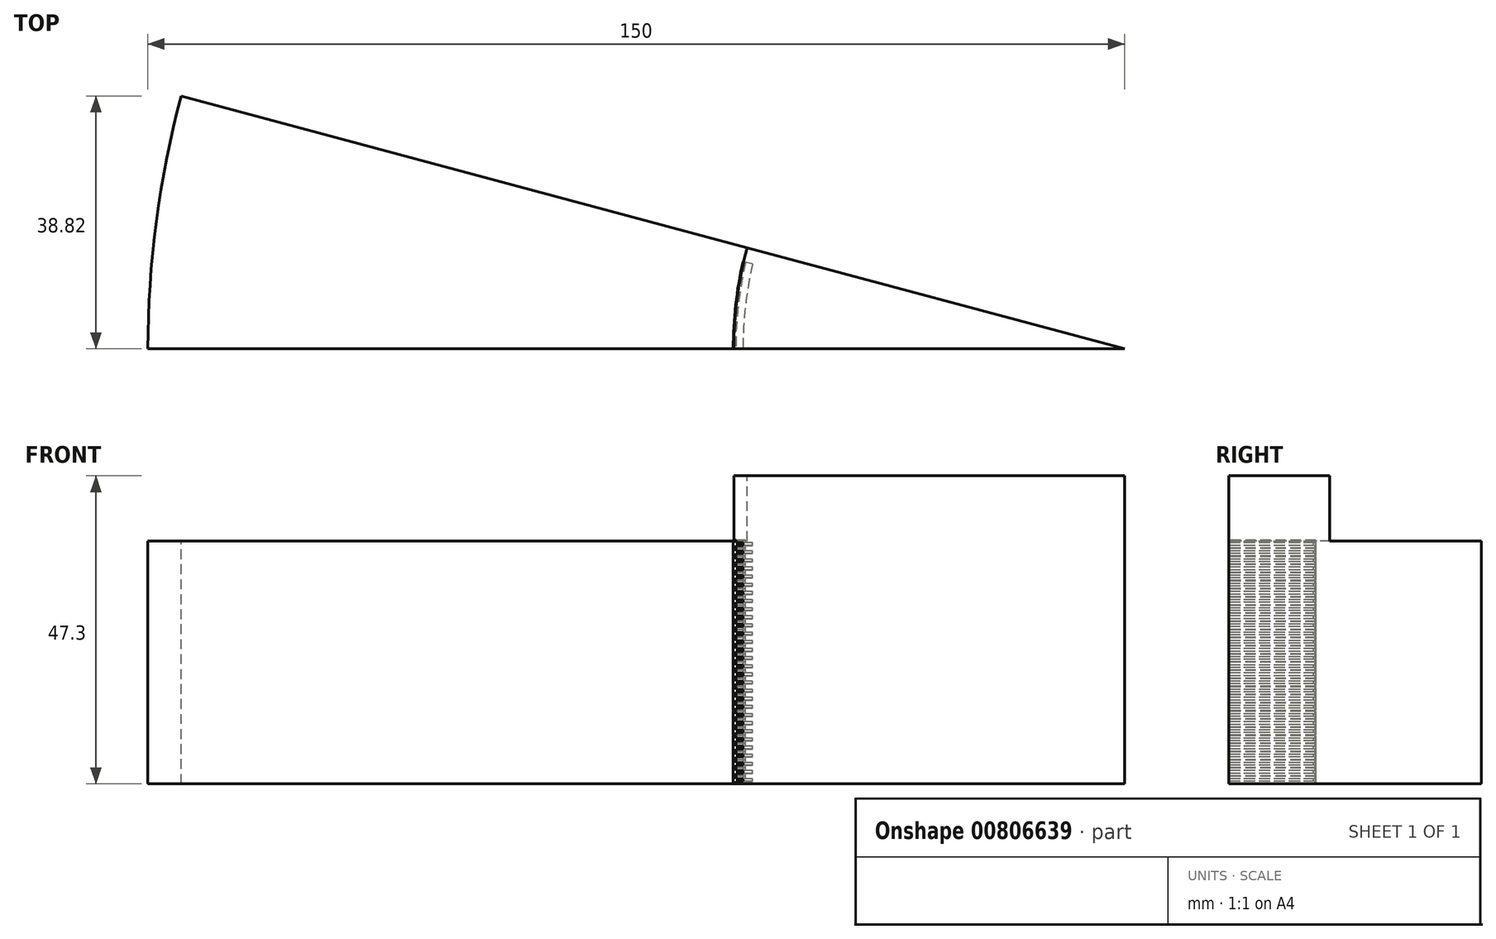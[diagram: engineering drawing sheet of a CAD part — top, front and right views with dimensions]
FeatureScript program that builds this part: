
annotation { "Feature Type Name" : "Feature", "Feature Type Description" : "" }
export const myFeature = defineFeature(function(context is Context, id is Id, definition is map)
    precondition{}
    {
        {
            var Q0;
            Q0=qCreatedBy(makeId("Front.planeOp"),FACE);
            var sketch = newSketch(context, id + "F0", { "sketchPlane" : qUnion([Q0])});
            skLineSegment(sketch, "E0", {"start": v(0, 0) * mm, "end": v(-150, 0) * mm});
            skLineSegment(sketch, "E1", {"start": v(-150, 0) * mm, "end": v(-150, 37.3) * mm});
            skLineSegment(sketch, "E2", {"start": v(-60, 37.3) * mm, "end": v(-60, 47.3) * mm});
            skLineSegment(sketch, "E3", {"start": v(-60, 47.3) * mm, "end": v(0, 47.3) * mm});
            skLineSegment(sketch, "E4", {"start": v(0, 47.3) * mm, "end": v(0, 0) * mm});
            skLineSegment(sketch, "E5", {"start": v(-150, 37.3) * mm, "end": v(-60, 37.3) * mm});
            skSolve(sketch);
        }
        {
            var Q0;
            Q0 = qSketchRegion(id + "F0", true);
            var Q1;
            Q1=sQuery(id+"F0.wireOp",EDGE,"E4");
            revolve(context, id + "F1", {"surfaceOperationType" : NewSurfaceOperationType.NEW, "entities" : qUnion([Q0]), "axis" : qUnion([Q1]), "revolveType" : RevolveType.ONE_DIRECTION, "angle" : 15 * degree});
        }
        {
            var Q0;
            Q0=makeQuery(id+"F1.opRevolve","CAP_FACE",FACE,{"disambiguationData":[OSD([sQuery(id+"F0.wireOp",EDGE,"E0"),sQuery(id+"F0.wireOp",EDGE,"E1"),sQuery(id+"F0.wireOp",EDGE,"E2"),sQuery(id+"F0.wireOp",EDGE,"E3"),sQuery(id+"F0.wireOp",EDGE,"E4"),sQuery(id+"F0.wireOp",EDGE,"E5")])],"isStart":true});
            var sketch = newSketch(context, id + "F2", { "sketchPlane" : qUnion([Q0])});
            skLineSegment(sketch, "E6", {"start": v(-60.1, 37.4) * mm, "end": v(-60.1, 36.23) * mm});
            skLineSegment(sketch, "E7", {"start": v(-60.1, 36.23) * mm, "end": v(-59.7, 36.23) * mm});
            skLineSegment(sketch, "E8", {"start": v(-59.7, 36.23) * mm, "end": v(-59.7, 36.61) * mm});
            skLineSegment(sketch, "E9", {"start": v(-59.7, 36.61) * mm, "end": v(-58.6, 36.61) * mm});
            skLineSegment(sketch, "E10", {"start": v(-58.6, 36.61) * mm, "end": v(-58.6, 37.01) * mm});
            skLineSegment(sketch, "E11", {"start": v(-58.6, 37.01) * mm, "end": v(-59.7, 37.01) * mm});
            skLineSegment(sketch, "E12", {"start": v(-59.7, 37.01) * mm, "end": v(-59.7, 37.4) * mm});
            skLineSegment(sketch, "E13", {"start": v(-59.7, 37.4) * mm, "end": v(-60.1, 37.4) * mm});
            skLineSegment(sketch, "E14.1.0.0", {"start": v(-59.7, 35.76) * mm, "end": v(-59.7, 36.15) * mm});
            skLineSegment(sketch, "E14.1.0.1", {"start": v(-58.6, 35.76) * mm, "end": v(-59.7, 35.76) * mm});
            skLineSegment(sketch, "E14.1.0.2", {"start": v(-58.6, 35.36) * mm, "end": v(-58.6, 35.76) * mm});
            skLineSegment(sketch, "E14.1.0.3", {"start": v(-59.7, 35.36) * mm, "end": v(-58.6, 35.36) * mm});
            skLineSegment(sketch, "E14.1.0.4", {"start": v(-59.7, 34.98) * mm, "end": v(-59.7, 35.36) * mm});
            skLineSegment(sketch, "E14.1.0.5", {"start": v(-60.1, 34.98) * mm, "end": v(-59.7, 34.98) * mm});
            skLineSegment(sketch, "E14.1.0.6", {"start": v(-60.1, 36.15) * mm, "end": v(-60.1, 34.98) * mm});
            skLineSegment(sketch, "E14.1.0.7", {"start": v(-59.7, 36.15) * mm, "end": v(-60.1, 36.15) * mm});
            skLineSegment(sketch, "E14.2.0.0", {"start": v(-59.7, 34.51) * mm, "end": v(-59.7, 34.9) * mm});
            skLineSegment(sketch, "E14.2.0.1", {"start": v(-58.6, 34.51) * mm, "end": v(-59.7, 34.51) * mm});
            skLineSegment(sketch, "E14.2.0.2", {"start": v(-58.6, 34.11) * mm, "end": v(-58.6, 34.51) * mm});
            skLineSegment(sketch, "E14.2.0.3", {"start": v(-59.7, 34.11) * mm, "end": v(-58.6, 34.11) * mm});
            skLineSegment(sketch, "E14.2.0.4", {"start": v(-59.7, 33.73) * mm, "end": v(-59.7, 34.11) * mm});
            skLineSegment(sketch, "E14.2.0.5", {"start": v(-60.1, 33.73) * mm, "end": v(-59.7, 33.73) * mm});
            skLineSegment(sketch, "E14.2.0.6", {"start": v(-60.1, 34.9) * mm, "end": v(-60.1, 33.73) * mm});
            skLineSegment(sketch, "E14.2.0.7", {"start": v(-59.7, 34.9) * mm, "end": v(-60.1, 34.9) * mm});
            skLineSegment(sketch, "E14.direction1", {"start": v(-60.1, 36.23) * mm, "end": v(-60.1, 34.98) * mm, "construction": true});
            skLineSegment(sketch, "E15.0.3.0", {"start": v(-59.7, 33.26) * mm, "end": v(-59.7, 33.65) * mm});
            skLineSegment(sketch, "E15.3.3.0", {"start": v(-58.6, 33.26) * mm, "end": v(-59.7, 33.26) * mm});
            skLineSegment(sketch, "E15.6.3.0", {"start": v(-58.6, 32.86) * mm, "end": v(-58.6, 33.26) * mm});
            skLineSegment(sketch, "E15.9.3.0", {"start": v(-59.7, 32.86) * mm, "end": v(-58.6, 32.86) * mm});
            skLineSegment(sketch, "E15.12.3.0", {"start": v(-59.7, 32.48) * mm, "end": v(-59.7, 32.86) * mm});
            skLineSegment(sketch, "E15.15.3.0", {"start": v(-60.1, 32.48) * mm, "end": v(-59.7, 32.48) * mm});
            skLineSegment(sketch, "E15.18.3.0", {"start": v(-60.1, 33.65) * mm, "end": v(-60.1, 32.48) * mm});
            skLineSegment(sketch, "E15.21.3.0", {"start": v(-59.7, 33.65) * mm, "end": v(-60.1, 33.65) * mm});
            skLineSegment(sketch, "E15.0.4.0", {"start": v(-59.7, 32.01) * mm, "end": v(-59.7, 32.4) * mm});
            skLineSegment(sketch, "E15.3.4.0", {"start": v(-58.6, 32.01) * mm, "end": v(-59.7, 32.01) * mm});
            skLineSegment(sketch, "E15.6.4.0", {"start": v(-58.6, 31.61) * mm, "end": v(-58.6, 32.01) * mm});
            skLineSegment(sketch, "E15.9.4.0", {"start": v(-59.7, 31.61) * mm, "end": v(-58.6, 31.61) * mm});
            skLineSegment(sketch, "E15.12.4.0", {"start": v(-59.7, 31.23) * mm, "end": v(-59.7, 31.61) * mm});
            skLineSegment(sketch, "E15.15.4.0", {"start": v(-60.1, 31.23) * mm, "end": v(-59.7, 31.23) * mm});
            skLineSegment(sketch, "E15.18.4.0", {"start": v(-60.1, 32.4) * mm, "end": v(-60.1, 31.23) * mm});
            skLineSegment(sketch, "E15.21.4.0", {"start": v(-59.7, 32.4) * mm, "end": v(-60.1, 32.4) * mm});
            skLineSegment(sketch, "E15.0.5.0", {"start": v(-59.7, 30.76) * mm, "end": v(-59.7, 31.15) * mm});
            skLineSegment(sketch, "E15.3.5.0", {"start": v(-58.6, 30.76) * mm, "end": v(-59.7, 30.76) * mm});
            skLineSegment(sketch, "E15.6.5.0", {"start": v(-58.6, 30.36) * mm, "end": v(-58.6, 30.76) * mm});
            skLineSegment(sketch, "E15.9.5.0", {"start": v(-59.7, 30.36) * mm, "end": v(-58.6, 30.36) * mm});
            skLineSegment(sketch, "E15.12.5.0", {"start": v(-59.7, 29.98) * mm, "end": v(-59.7, 30.36) * mm});
            skLineSegment(sketch, "E15.15.5.0", {"start": v(-60.1, 29.98) * mm, "end": v(-59.7, 29.98) * mm});
            skLineSegment(sketch, "E15.18.5.0", {"start": v(-60.1, 31.15) * mm, "end": v(-60.1, 29.98) * mm});
            skLineSegment(sketch, "E15.21.5.0", {"start": v(-59.7, 31.15) * mm, "end": v(-60.1, 31.15) * mm});
            skLineSegment(sketch, "E15.0.6.0", {"start": v(-59.7, 29.51) * mm, "end": v(-59.7, 29.9) * mm});
            skLineSegment(sketch, "E15.3.6.0", {"start": v(-58.6, 29.51) * mm, "end": v(-59.7, 29.51) * mm});
            skLineSegment(sketch, "E15.6.6.0", {"start": v(-58.6, 29.11) * mm, "end": v(-58.6, 29.51) * mm});
            skLineSegment(sketch, "E15.9.6.0", {"start": v(-59.7, 29.11) * mm, "end": v(-58.6, 29.11) * mm});
            skLineSegment(sketch, "E15.12.6.0", {"start": v(-59.7, 28.73) * mm, "end": v(-59.7, 29.11) * mm});
            skLineSegment(sketch, "E15.15.6.0", {"start": v(-60.1, 28.73) * mm, "end": v(-59.7, 28.73) * mm});
            skLineSegment(sketch, "E15.18.6.0", {"start": v(-60.1, 29.9) * mm, "end": v(-60.1, 28.73) * mm});
            skLineSegment(sketch, "E15.21.6.0", {"start": v(-59.7, 29.9) * mm, "end": v(-60.1, 29.9) * mm});
            skLineSegment(sketch, "E15.0.7.0", {"start": v(-59.7, 28.26) * mm, "end": v(-59.7, 28.65) * mm});
            skLineSegment(sketch, "E15.3.7.0", {"start": v(-58.6, 28.26) * mm, "end": v(-59.7, 28.26) * mm});
            skLineSegment(sketch, "E15.6.7.0", {"start": v(-58.6, 27.86) * mm, "end": v(-58.6, 28.26) * mm});
            skLineSegment(sketch, "E15.9.7.0", {"start": v(-59.7, 27.86) * mm, "end": v(-58.6, 27.86) * mm});
            skLineSegment(sketch, "E15.12.7.0", {"start": v(-59.7, 27.48) * mm, "end": v(-59.7, 27.86) * mm});
            skLineSegment(sketch, "E15.15.7.0", {"start": v(-60.1, 27.48) * mm, "end": v(-59.7, 27.48) * mm});
            skLineSegment(sketch, "E15.18.7.0", {"start": v(-60.1, 28.65) * mm, "end": v(-60.1, 27.48) * mm});
            skLineSegment(sketch, "E15.21.7.0", {"start": v(-59.7, 28.65) * mm, "end": v(-60.1, 28.65) * mm});
            skLineSegment(sketch, "E15.0.8.0", {"start": v(-59.7, 27.01) * mm, "end": v(-59.7, 27.4) * mm});
            skLineSegment(sketch, "E15.3.8.0", {"start": v(-58.6, 27.01) * mm, "end": v(-59.7, 27.01) * mm});
            skLineSegment(sketch, "E15.6.8.0", {"start": v(-58.6, 26.61) * mm, "end": v(-58.6, 27.01) * mm});
            skLineSegment(sketch, "E15.9.8.0", {"start": v(-59.7, 26.61) * mm, "end": v(-58.6, 26.61) * mm});
            skLineSegment(sketch, "E15.12.8.0", {"start": v(-59.7, 26.23) * mm, "end": v(-59.7, 26.61) * mm});
            skLineSegment(sketch, "E15.15.8.0", {"start": v(-60.1, 26.23) * mm, "end": v(-59.7, 26.23) * mm});
            skLineSegment(sketch, "E15.18.8.0", {"start": v(-60.1, 27.4) * mm, "end": v(-60.1, 26.23) * mm});
            skLineSegment(sketch, "E15.21.8.0", {"start": v(-59.7, 27.4) * mm, "end": v(-60.1, 27.4) * mm});
            skLineSegment(sketch, "E15.0.9.0", {"start": v(-59.7, 25.76) * mm, "end": v(-59.7, 26.15) * mm});
            skLineSegment(sketch, "E15.3.9.0", {"start": v(-58.6, 25.76) * mm, "end": v(-59.7, 25.76) * mm});
            skLineSegment(sketch, "E15.6.9.0", {"start": v(-58.6, 25.36) * mm, "end": v(-58.6, 25.76) * mm});
            skLineSegment(sketch, "E15.9.9.0", {"start": v(-59.7, 25.36) * mm, "end": v(-58.6, 25.36) * mm});
            skLineSegment(sketch, "E15.12.9.0", {"start": v(-59.7, 24.98) * mm, "end": v(-59.7, 25.36) * mm});
            skLineSegment(sketch, "E15.15.9.0", {"start": v(-60.1, 24.98) * mm, "end": v(-59.7, 24.98) * mm});
            skLineSegment(sketch, "E15.18.9.0", {"start": v(-60.1, 26.15) * mm, "end": v(-60.1, 24.98) * mm});
            skLineSegment(sketch, "E15.21.9.0", {"start": v(-59.7, 26.15) * mm, "end": v(-60.1, 26.15) * mm});
            skLineSegment(sketch, "E16.0.10.0", {"start": v(-59.7, 24.51) * mm, "end": v(-59.7, 24.9) * mm});
            skLineSegment(sketch, "E16.3.10.0", {"start": v(-58.6, 24.51) * mm, "end": v(-59.7, 24.51) * mm});
            skLineSegment(sketch, "E16.6.10.0", {"start": v(-58.6, 24.11) * mm, "end": v(-58.6, 24.51) * mm});
            skLineSegment(sketch, "E16.9.10.0", {"start": v(-59.7, 24.11) * mm, "end": v(-58.6, 24.11) * mm});
            skLineSegment(sketch, "E16.12.10.0", {"start": v(-59.7, 23.73) * mm, "end": v(-59.7, 24.11) * mm});
            skLineSegment(sketch, "E16.15.10.0", {"start": v(-60.1, 23.73) * mm, "end": v(-59.7, 23.73) * mm});
            skLineSegment(sketch, "E16.18.10.0", {"start": v(-60.1, 24.9) * mm, "end": v(-60.1, 23.73) * mm});
            skLineSegment(sketch, "E16.21.10.0", {"start": v(-59.7, 24.9) * mm, "end": v(-60.1, 24.9) * mm});
            skLineSegment(sketch, "E16.0.11.0", {"start": v(-59.7, 23.26) * mm, "end": v(-59.7, 23.65) * mm});
            skLineSegment(sketch, "E16.3.11.0", {"start": v(-58.6, 23.26) * mm, "end": v(-59.7, 23.26) * mm});
            skLineSegment(sketch, "E16.6.11.0", {"start": v(-58.6, 22.86) * mm, "end": v(-58.6, 23.26) * mm});
            skLineSegment(sketch, "E16.9.11.0", {"start": v(-59.7, 22.86) * mm, "end": v(-58.6, 22.86) * mm});
            skLineSegment(sketch, "E16.12.11.0", {"start": v(-59.7, 22.48) * mm, "end": v(-59.7, 22.86) * mm});
            skLineSegment(sketch, "E16.15.11.0", {"start": v(-60.1, 22.48) * mm, "end": v(-59.7, 22.48) * mm});
            skLineSegment(sketch, "E16.18.11.0", {"start": v(-60.1, 23.65) * mm, "end": v(-60.1, 22.48) * mm});
            skLineSegment(sketch, "E16.21.11.0", {"start": v(-59.7, 23.65) * mm, "end": v(-60.1, 23.65) * mm});
            skLineSegment(sketch, "E16.0.12.0", {"start": v(-59.7, 22.01) * mm, "end": v(-59.7, 22.4) * mm});
            skLineSegment(sketch, "E16.3.12.0", {"start": v(-58.6, 22.01) * mm, "end": v(-59.7, 22.01) * mm});
            skLineSegment(sketch, "E16.6.12.0", {"start": v(-58.6, 21.61) * mm, "end": v(-58.6, 22.01) * mm});
            skLineSegment(sketch, "E16.9.12.0", {"start": v(-59.7, 21.61) * mm, "end": v(-58.6, 21.61) * mm});
            skLineSegment(sketch, "E16.12.12.0", {"start": v(-59.7, 21.23) * mm, "end": v(-59.7, 21.61) * mm});
            skLineSegment(sketch, "E16.15.12.0", {"start": v(-60.1, 21.23) * mm, "end": v(-59.7, 21.23) * mm});
            skLineSegment(sketch, "E16.18.12.0", {"start": v(-60.1, 22.4) * mm, "end": v(-60.1, 21.23) * mm});
            skLineSegment(sketch, "E16.21.12.0", {"start": v(-59.7, 22.4) * mm, "end": v(-60.1, 22.4) * mm});
            skLineSegment(sketch, "E16.0.13.0", {"start": v(-59.7, 20.76) * mm, "end": v(-59.7, 21.15) * mm});
            skLineSegment(sketch, "E16.3.13.0", {"start": v(-58.6, 20.76) * mm, "end": v(-59.7, 20.76) * mm});
            skLineSegment(sketch, "E16.6.13.0", {"start": v(-58.6, 20.36) * mm, "end": v(-58.6, 20.76) * mm});
            skLineSegment(sketch, "E16.9.13.0", {"start": v(-59.7, 20.36) * mm, "end": v(-58.6, 20.36) * mm});
            skLineSegment(sketch, "E16.12.13.0", {"start": v(-59.7, 19.98) * mm, "end": v(-59.7, 20.36) * mm});
            skLineSegment(sketch, "E16.15.13.0", {"start": v(-60.1, 19.98) * mm, "end": v(-59.7, 19.98) * mm});
            skLineSegment(sketch, "E16.18.13.0", {"start": v(-60.1, 21.15) * mm, "end": v(-60.1, 19.98) * mm});
            skLineSegment(sketch, "E16.21.13.0", {"start": v(-59.7, 21.15) * mm, "end": v(-60.1, 21.15) * mm});
            skLineSegment(sketch, "E16.0.14.0", {"start": v(-59.7, 19.51) * mm, "end": v(-59.7, 19.9) * mm});
            skLineSegment(sketch, "E16.3.14.0", {"start": v(-58.6, 19.51) * mm, "end": v(-59.7, 19.51) * mm});
            skLineSegment(sketch, "E16.6.14.0", {"start": v(-58.6, 19.11) * mm, "end": v(-58.6, 19.51) * mm});
            skLineSegment(sketch, "E16.9.14.0", {"start": v(-59.7, 19.11) * mm, "end": v(-58.6, 19.11) * mm});
            skLineSegment(sketch, "E16.12.14.0", {"start": v(-59.7, 18.73) * mm, "end": v(-59.7, 19.11) * mm});
            skLineSegment(sketch, "E16.15.14.0", {"start": v(-60.1, 18.73) * mm, "end": v(-59.7, 18.73) * mm});
            skLineSegment(sketch, "E16.18.14.0", {"start": v(-60.1, 19.9) * mm, "end": v(-60.1, 18.73) * mm});
            skLineSegment(sketch, "E16.21.14.0", {"start": v(-59.7, 19.9) * mm, "end": v(-60.1, 19.9) * mm});
            skLineSegment(sketch, "E16.0.15.0", {"start": v(-59.7, 18.26) * mm, "end": v(-59.7, 18.65) * mm});
            skLineSegment(sketch, "E16.3.15.0", {"start": v(-58.6, 18.26) * mm, "end": v(-59.7, 18.26) * mm});
            skLineSegment(sketch, "E16.6.15.0", {"start": v(-58.6, 17.86) * mm, "end": v(-58.6, 18.26) * mm});
            skLineSegment(sketch, "E16.9.15.0", {"start": v(-59.7, 17.86) * mm, "end": v(-58.6, 17.86) * mm});
            skLineSegment(sketch, "E16.12.15.0", {"start": v(-59.7, 17.48) * mm, "end": v(-59.7, 17.86) * mm});
            skLineSegment(sketch, "E16.15.15.0", {"start": v(-60.1, 17.48) * mm, "end": v(-59.7, 17.48) * mm});
            skLineSegment(sketch, "E16.18.15.0", {"start": v(-60.1, 18.65) * mm, "end": v(-60.1, 17.48) * mm});
            skLineSegment(sketch, "E16.21.15.0", {"start": v(-59.7, 18.65) * mm, "end": v(-60.1, 18.65) * mm});
            skLineSegment(sketch, "E16.0.16.0", {"start": v(-59.7, 17.01) * mm, "end": v(-59.7, 17.4) * mm});
            skLineSegment(sketch, "E16.3.16.0", {"start": v(-58.6, 17.01) * mm, "end": v(-59.7, 17.01) * mm});
            skLineSegment(sketch, "E16.6.16.0", {"start": v(-58.6, 16.61) * mm, "end": v(-58.6, 17.01) * mm});
            skLineSegment(sketch, "E16.9.16.0", {"start": v(-59.7, 16.61) * mm, "end": v(-58.6, 16.61) * mm});
            skLineSegment(sketch, "E16.12.16.0", {"start": v(-59.7, 16.23) * mm, "end": v(-59.7, 16.61) * mm});
            skLineSegment(sketch, "E16.15.16.0", {"start": v(-60.1, 16.23) * mm, "end": v(-59.7, 16.23) * mm});
            skLineSegment(sketch, "E16.18.16.0", {"start": v(-60.1, 17.4) * mm, "end": v(-60.1, 16.23) * mm});
            skLineSegment(sketch, "E16.21.16.0", {"start": v(-59.7, 17.4) * mm, "end": v(-60.1, 17.4) * mm});
            skLineSegment(sketch, "E16.0.17.0", {"start": v(-59.7, 15.76) * mm, "end": v(-59.7, 16.15) * mm});
            skLineSegment(sketch, "E16.3.17.0", {"start": v(-58.6, 15.76) * mm, "end": v(-59.7, 15.76) * mm});
            skLineSegment(sketch, "E16.6.17.0", {"start": v(-58.6, 15.36) * mm, "end": v(-58.6, 15.76) * mm});
            skLineSegment(sketch, "E16.9.17.0", {"start": v(-59.7, 15.36) * mm, "end": v(-58.6, 15.36) * mm});
            skLineSegment(sketch, "E16.12.17.0", {"start": v(-59.7, 14.98) * mm, "end": v(-59.7, 15.36) * mm});
            skLineSegment(sketch, "E16.15.17.0", {"start": v(-60.1, 14.98) * mm, "end": v(-59.7, 14.98) * mm});
            skLineSegment(sketch, "E16.18.17.0", {"start": v(-60.1, 16.15) * mm, "end": v(-60.1, 14.98) * mm});
            skLineSegment(sketch, "E16.21.17.0", {"start": v(-59.7, 16.15) * mm, "end": v(-60.1, 16.15) * mm});
            skLineSegment(sketch, "E16.0.18.0", {"start": v(-59.7, 14.51) * mm, "end": v(-59.7, 14.9) * mm});
            skLineSegment(sketch, "E16.3.18.0", {"start": v(-58.6, 14.51) * mm, "end": v(-59.7, 14.51) * mm});
            skLineSegment(sketch, "E16.6.18.0", {"start": v(-58.6, 14.11) * mm, "end": v(-58.6, 14.51) * mm});
            skLineSegment(sketch, "E16.9.18.0", {"start": v(-59.7, 14.11) * mm, "end": v(-58.6, 14.11) * mm});
            skLineSegment(sketch, "E16.12.18.0", {"start": v(-59.7, 13.73) * mm, "end": v(-59.7, 14.11) * mm});
            skLineSegment(sketch, "E16.15.18.0", {"start": v(-60.1, 13.73) * mm, "end": v(-59.7, 13.73) * mm});
            skLineSegment(sketch, "E16.18.18.0", {"start": v(-60.1, 14.9) * mm, "end": v(-60.1, 13.73) * mm});
            skLineSegment(sketch, "E16.21.18.0", {"start": v(-59.7, 14.9) * mm, "end": v(-60.1, 14.9) * mm});
            skLineSegment(sketch, "E16.0.19.0", {"start": v(-59.7, 13.26) * mm, "end": v(-59.7, 13.65) * mm});
            skLineSegment(sketch, "E16.3.19.0", {"start": v(-58.6, 13.26) * mm, "end": v(-59.7, 13.26) * mm});
            skLineSegment(sketch, "E16.6.19.0", {"start": v(-58.6, 12.86) * mm, "end": v(-58.6, 13.26) * mm});
            skLineSegment(sketch, "E16.9.19.0", {"start": v(-59.7, 12.86) * mm, "end": v(-58.6, 12.86) * mm});
            skLineSegment(sketch, "E16.12.19.0", {"start": v(-59.7, 12.48) * mm, "end": v(-59.7, 12.86) * mm});
            skLineSegment(sketch, "E16.15.19.0", {"start": v(-60.1, 12.48) * mm, "end": v(-59.7, 12.48) * mm});
            skLineSegment(sketch, "E16.18.19.0", {"start": v(-60.1, 13.65) * mm, "end": v(-60.1, 12.48) * mm});
            skLineSegment(sketch, "E16.21.19.0", {"start": v(-59.7, 13.65) * mm, "end": v(-60.1, 13.65) * mm});
            skLineSegment(sketch, "E16.0.20.0", {"start": v(-59.7, 12.01) * mm, "end": v(-59.7, 12.4) * mm});
            skLineSegment(sketch, "E16.3.20.0", {"start": v(-58.6, 12.01) * mm, "end": v(-59.7, 12.01) * mm});
            skLineSegment(sketch, "E16.6.20.0", {"start": v(-58.6, 11.61) * mm, "end": v(-58.6, 12.01) * mm});
            skLineSegment(sketch, "E16.9.20.0", {"start": v(-59.7, 11.61) * mm, "end": v(-58.6, 11.61) * mm});
            skLineSegment(sketch, "E16.12.20.0", {"start": v(-59.7, 11.23) * mm, "end": v(-59.7, 11.61) * mm});
            skLineSegment(sketch, "E16.15.20.0", {"start": v(-60.1, 11.23) * mm, "end": v(-59.7, 11.23) * mm});
            skLineSegment(sketch, "E16.18.20.0", {"start": v(-60.1, 12.4) * mm, "end": v(-60.1, 11.23) * mm});
            skLineSegment(sketch, "E16.21.20.0", {"start": v(-59.7, 12.4) * mm, "end": v(-60.1, 12.4) * mm});
            skLineSegment(sketch, "E16.0.21.0", {"start": v(-59.7, 10.76) * mm, "end": v(-59.7, 11.15) * mm});
            skLineSegment(sketch, "E16.3.21.0", {"start": v(-58.6, 10.76) * mm, "end": v(-59.7, 10.76) * mm});
            skLineSegment(sketch, "E16.6.21.0", {"start": v(-58.6, 10.36) * mm, "end": v(-58.6, 10.76) * mm});
            skLineSegment(sketch, "E16.9.21.0", {"start": v(-59.7, 10.36) * mm, "end": v(-58.6, 10.36) * mm});
            skLineSegment(sketch, "E16.12.21.0", {"start": v(-59.7, 9.98) * mm, "end": v(-59.7, 10.36) * mm});
            skLineSegment(sketch, "E16.15.21.0", {"start": v(-60.1, 9.98) * mm, "end": v(-59.7, 9.98) * mm});
            skLineSegment(sketch, "E16.18.21.0", {"start": v(-60.1, 11.15) * mm, "end": v(-60.1, 9.98) * mm});
            skLineSegment(sketch, "E16.21.21.0", {"start": v(-59.7, 11.15) * mm, "end": v(-60.1, 11.15) * mm});
            skLineSegment(sketch, "E16.0.22.0", {"start": v(-59.7, 9.51) * mm, "end": v(-59.7, 9.9) * mm});
            skLineSegment(sketch, "E16.3.22.0", {"start": v(-58.6, 9.51) * mm, "end": v(-59.7, 9.51) * mm});
            skLineSegment(sketch, "E16.6.22.0", {"start": v(-58.6, 9.11) * mm, "end": v(-58.6, 9.51) * mm});
            skLineSegment(sketch, "E16.9.22.0", {"start": v(-59.7, 9.11) * mm, "end": v(-58.6, 9.11) * mm});
            skLineSegment(sketch, "E16.12.22.0", {"start": v(-59.7, 8.73) * mm, "end": v(-59.7, 9.11) * mm});
            skLineSegment(sketch, "E16.15.22.0", {"start": v(-60.1, 8.73) * mm, "end": v(-59.7, 8.73) * mm});
            skLineSegment(sketch, "E16.18.22.0", {"start": v(-60.1, 9.9) * mm, "end": v(-60.1, 8.73) * mm});
            skLineSegment(sketch, "E16.21.22.0", {"start": v(-59.7, 9.9) * mm, "end": v(-60.1, 9.9) * mm});
            skLineSegment(sketch, "E16.0.23.0", {"start": v(-59.7, 8.26) * mm, "end": v(-59.7, 8.65) * mm});
            skLineSegment(sketch, "E16.3.23.0", {"start": v(-58.6, 8.26) * mm, "end": v(-59.7, 8.26) * mm});
            skLineSegment(sketch, "E16.6.23.0", {"start": v(-58.6, 7.86) * mm, "end": v(-58.6, 8.26) * mm});
            skLineSegment(sketch, "E16.9.23.0", {"start": v(-59.7, 7.86) * mm, "end": v(-58.6, 7.86) * mm});
            skLineSegment(sketch, "E16.12.23.0", {"start": v(-59.7, 7.48) * mm, "end": v(-59.7, 7.86) * mm});
            skLineSegment(sketch, "E16.15.23.0", {"start": v(-60.1, 7.48) * mm, "end": v(-59.7, 7.48) * mm});
            skLineSegment(sketch, "E16.18.23.0", {"start": v(-60.1, 8.65) * mm, "end": v(-60.1, 7.48) * mm});
            skLineSegment(sketch, "E16.21.23.0", {"start": v(-59.7, 8.65) * mm, "end": v(-60.1, 8.65) * mm});
            skLineSegment(sketch, "E16.0.24.0", {"start": v(-59.7, 7.01) * mm, "end": v(-59.7, 7.4) * mm});
            skLineSegment(sketch, "E16.3.24.0", {"start": v(-58.6, 7.01) * mm, "end": v(-59.7, 7.01) * mm});
            skLineSegment(sketch, "E16.6.24.0", {"start": v(-58.6, 6.61) * mm, "end": v(-58.6, 7.01) * mm});
            skLineSegment(sketch, "E16.9.24.0", {"start": v(-59.7, 6.61) * mm, "end": v(-58.6, 6.61) * mm});
            skLineSegment(sketch, "E16.12.24.0", {"start": v(-59.7, 6.23) * mm, "end": v(-59.7, 6.61) * mm});
            skLineSegment(sketch, "E16.15.24.0", {"start": v(-60.1, 6.23) * mm, "end": v(-59.7, 6.23) * mm});
            skLineSegment(sketch, "E16.18.24.0", {"start": v(-60.1, 7.4) * mm, "end": v(-60.1, 6.23) * mm});
            skLineSegment(sketch, "E16.21.24.0", {"start": v(-59.7, 7.4) * mm, "end": v(-60.1, 7.4) * mm});
            skLineSegment(sketch, "E16.0.25.0", {"start": v(-59.7, 5.76) * mm, "end": v(-59.7, 6.15) * mm});
            skLineSegment(sketch, "E16.3.25.0", {"start": v(-58.6, 5.76) * mm, "end": v(-59.7, 5.76) * mm});
            skLineSegment(sketch, "E16.6.25.0", {"start": v(-58.6, 5.36) * mm, "end": v(-58.6, 5.76) * mm});
            skLineSegment(sketch, "E16.9.25.0", {"start": v(-59.7, 5.36) * mm, "end": v(-58.6, 5.36) * mm});
            skLineSegment(sketch, "E16.12.25.0", {"start": v(-59.7, 4.98) * mm, "end": v(-59.7, 5.36) * mm});
            skLineSegment(sketch, "E16.15.25.0", {"start": v(-60.1, 4.98) * mm, "end": v(-59.7, 4.98) * mm});
            skLineSegment(sketch, "E16.18.25.0", {"start": v(-60.1, 6.15) * mm, "end": v(-60.1, 4.98) * mm});
            skLineSegment(sketch, "E16.21.25.0", {"start": v(-59.7, 6.15) * mm, "end": v(-60.1, 6.15) * mm});
            skLineSegment(sketch, "E16.0.26.0", {"start": v(-59.7, 4.51) * mm, "end": v(-59.7, 4.9) * mm});
            skLineSegment(sketch, "E16.3.26.0", {"start": v(-58.6, 4.51) * mm, "end": v(-59.7, 4.51) * mm});
            skLineSegment(sketch, "E16.6.26.0", {"start": v(-58.6, 4.11) * mm, "end": v(-58.6, 4.51) * mm});
            skLineSegment(sketch, "E16.9.26.0", {"start": v(-59.7, 4.11) * mm, "end": v(-58.6, 4.11) * mm});
            skLineSegment(sketch, "E16.12.26.0", {"start": v(-59.7, 3.73) * mm, "end": v(-59.7, 4.11) * mm});
            skLineSegment(sketch, "E16.15.26.0", {"start": v(-60.1, 3.73) * mm, "end": v(-59.7, 3.73) * mm});
            skLineSegment(sketch, "E16.18.26.0", {"start": v(-60.1, 4.9) * mm, "end": v(-60.1, 3.73) * mm});
            skLineSegment(sketch, "E16.21.26.0", {"start": v(-59.7, 4.9) * mm, "end": v(-60.1, 4.9) * mm});
            skLineSegment(sketch, "E16.0.27.0", {"start": v(-59.7, 3.26) * mm, "end": v(-59.7, 3.65) * mm});
            skLineSegment(sketch, "E16.3.27.0", {"start": v(-58.6, 3.26) * mm, "end": v(-59.7, 3.26) * mm});
            skLineSegment(sketch, "E16.6.27.0", {"start": v(-58.6, 2.86) * mm, "end": v(-58.6, 3.26) * mm});
            skLineSegment(sketch, "E16.9.27.0", {"start": v(-59.7, 2.86) * mm, "end": v(-58.6, 2.86) * mm});
            skLineSegment(sketch, "E16.12.27.0", {"start": v(-59.7, 2.48) * mm, "end": v(-59.7, 2.86) * mm});
            skLineSegment(sketch, "E16.15.27.0", {"start": v(-60.1, 2.48) * mm, "end": v(-59.7, 2.48) * mm});
            skLineSegment(sketch, "E16.18.27.0", {"start": v(-60.1, 3.65) * mm, "end": v(-60.1, 2.48) * mm});
            skLineSegment(sketch, "E16.21.27.0", {"start": v(-59.7, 3.65) * mm, "end": v(-60.1, 3.65) * mm});
            skLineSegment(sketch, "E16.0.28.0", {"start": v(-59.7, 2.01) * mm, "end": v(-59.7, 2.4) * mm});
            skLineSegment(sketch, "E16.3.28.0", {"start": v(-58.6, 2.01) * mm, "end": v(-59.7, 2.01) * mm});
            skLineSegment(sketch, "E16.6.28.0", {"start": v(-58.6, 1.61) * mm, "end": v(-58.6, 2.01) * mm});
            skLineSegment(sketch, "E16.9.28.0", {"start": v(-59.7, 1.61) * mm, "end": v(-58.6, 1.61) * mm});
            skLineSegment(sketch, "E16.12.28.0", {"start": v(-59.7, 1.23) * mm, "end": v(-59.7, 1.61) * mm});
            skLineSegment(sketch, "E16.15.28.0", {"start": v(-60.1, 1.23) * mm, "end": v(-59.7, 1.23) * mm});
            skLineSegment(sketch, "E16.18.28.0", {"start": v(-60.1, 2.4) * mm, "end": v(-60.1, 1.23) * mm});
            skLineSegment(sketch, "E16.21.28.0", {"start": v(-59.7, 2.4) * mm, "end": v(-60.1, 2.4) * mm});
            skLineSegment(sketch, "E16.0.29.0", {"start": v(-59.7, 0.76) * mm, "end": v(-59.7, 1.15) * mm});
            skLineSegment(sketch, "E16.3.29.0", {"start": v(-58.6, 0.76) * mm, "end": v(-59.7, 0.76) * mm});
            skLineSegment(sketch, "E16.6.29.0", {"start": v(-58.6, 0.36) * mm, "end": v(-58.6, 0.76) * mm});
            skLineSegment(sketch, "E16.9.29.0", {"start": v(-59.7, 0.36) * mm, "end": v(-58.6, 0.36) * mm});
            skLineSegment(sketch, "E16.12.29.0", {"start": v(-59.7, -0.02) * mm, "end": v(-59.7, 0.36) * mm});
            skLineSegment(sketch, "E16.15.29.0", {"start": v(-60.1, -0.02) * mm, "end": v(-59.7, -0.02) * mm});
            skLineSegment(sketch, "E16.18.29.0", {"start": v(-60.1, 1.15) * mm, "end": v(-60.1, -0.02) * mm});
            skLineSegment(sketch, "E16.21.29.0", {"start": v(-59.7, 1.15) * mm, "end": v(-60.1, 1.15) * mm});
            skSolve(sketch);
        }
        {
            var Q0;
            Q0 = qSketchRegion(id + "F2", true);
            var Q1;
            Q1=makeQuery(id+"F1.opRevolve","CAP_EDGE",EDGE,{"disambiguationData":[OSD([sQuery(id+"F0.wireOp",EDGE,"E4")])],"isStart":true});
            revolve(context, id + "F3", {"operationType" : NewBodyOperationType.REMOVE, "surfaceOperationType" : NewSurfaceOperationType.NEW, "entities" : qUnion([Q0]), "axis" : qUnion([Q1]), "revolveType" : RevolveType.ONE_DIRECTION, "angle" : 12.85 * degree});
        }
    });
